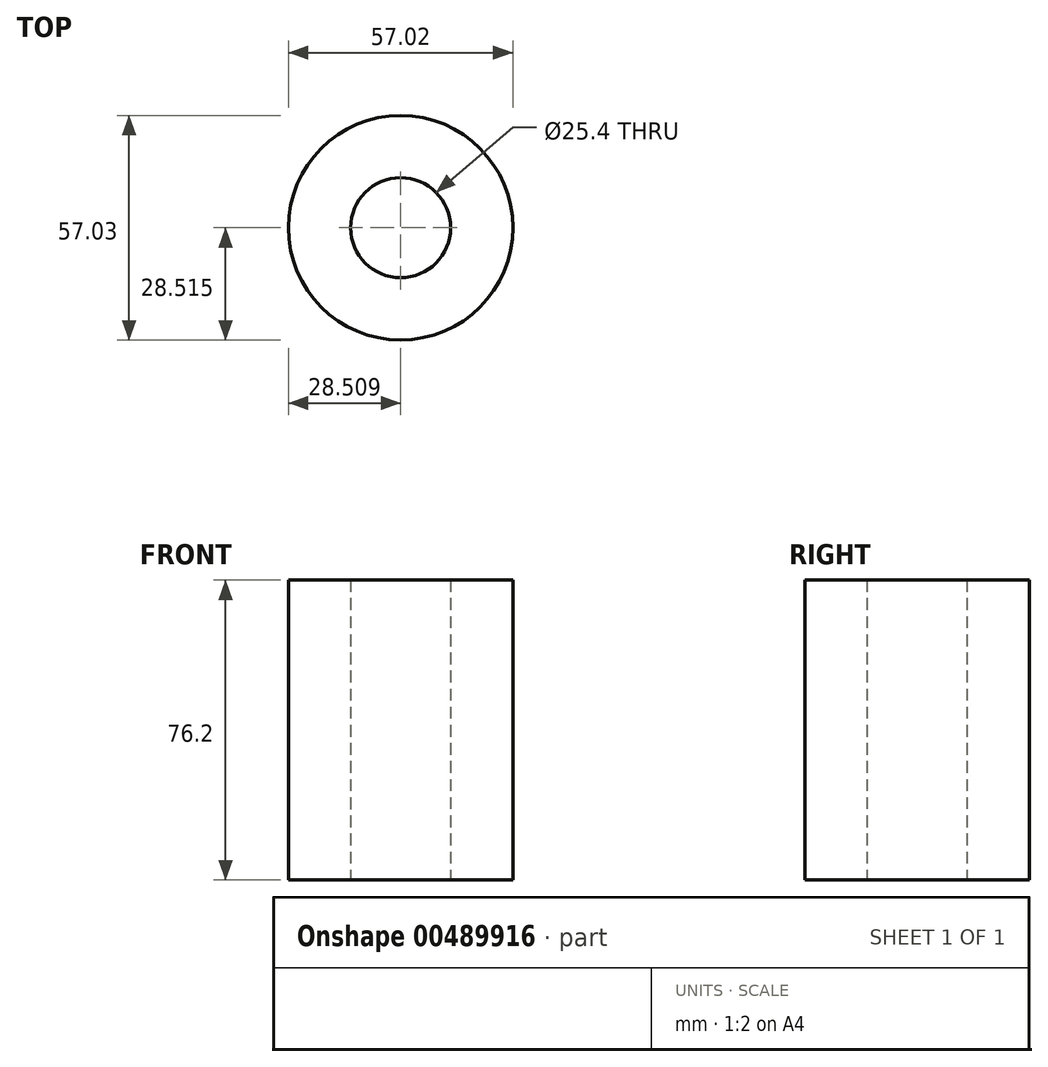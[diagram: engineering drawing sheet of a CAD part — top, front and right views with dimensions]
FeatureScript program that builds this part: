
annotation { "Feature Type Name" : "Feature", "Feature Type Description" : "" }
export const myFeature = defineFeature(function(context is Context, id is Id, definition is map)
    precondition{}
    {
        {
            var Q0;
            Q0=qCreatedBy(makeId("Top.planeOp"),FACE);
            var sketch = newSketch(context, id + "F0", { "sketchPlane" : qUnion([Q0])});
            skCircle(sketch, "E0", {"center": v(-119.2, 26.13) * mm, "radius": 28.51 * mm});
            skSolve(sketch);
        }
        {
            var Q0;
            Q0 = qSketchRegion(id + "F0", true);
            extrude(context, id + "F1", {"entities" : qUnion([Q0]), "depth" : 76.2 * mm});
        }
        {
            var Q0;
            Q0=sQuery(id+"F0.wireOp",VERTEX,"E0.center");
            var Q1;
            Q1=makeQuery(id+"F1.opExtrude","SWEPT_BODY",BODY,{"disambiguationData":[OSD([sQuery(id+"F0.wireOp",EDGE,"E0")])]});
            hole(context, id + "F2", {"style" : HoleStyle.SIMPLE, "endStyle" : HoleEndStyle.THROUGH, "oppositeDirection" : true, "holeDiameter" : 25.4 * mm, "isTappedThrough" : true, "tappedDepth" : 12.7 * mm, "tapClearance" : 3, "locations" : qUnion([Q0]), "scope" : qUnion([Q1])});
        }
    });
